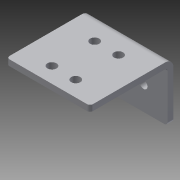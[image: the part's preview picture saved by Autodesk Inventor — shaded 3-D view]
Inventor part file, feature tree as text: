
AUTODESK INVENTOR PART (.ipt)
format: ipt  version: 2014 (Build 180170000, 170)  size: 136,192 bytes
history: native  units: in
note: dims shown in document units (in); Inventor stores cm internally (conversion verified against a paired STEP export)
features: sheet_metal_op x4, sketch x3, other x2, fillet x1, extrude x1
ambient origin geometry x8: Origin, YZ Plane, XZ Plane, XY Plane, X Axis, Y Axis, Z Axis, Center Point
bodies: Solid1 (feature_tree)
feature tree (11):
  sheet_metal_op  "Face1"
  sheet_metal_op  "Flange1"
  fillet  "Fillet1"  Radius=1.75in
  extrude  "Extrusion1"  Depth=0.163in
  sketch  "Sketch1"  dims[d1=1.0in d2=0.163in]
  other  "Plate1"
  sketch  "Sketch2"  dims[d4=0.7874in d6=1.0in d7=0.3937in d9=1.0in]
  other  "Plate2"
  sheet_metal_op  "Bend1"
  sheet_metal_op  "Corner1"
  sketch  "Sketch3"  dims[d11=0.125in d12=0.125in d13=0.0625in d14=0.25in d15=0.125in d16=1.75in d17=90.0deg d18=0.05in d19=0.5in d20=0.125in d21=0.125in d22=0.0625in d23=1.35in d24=0.75in d25=0.125in d27=0.19in d28=0.125in d29=0.2265in d30=1.0in d31=0.0in d34=0.5in d35=0.25in]
